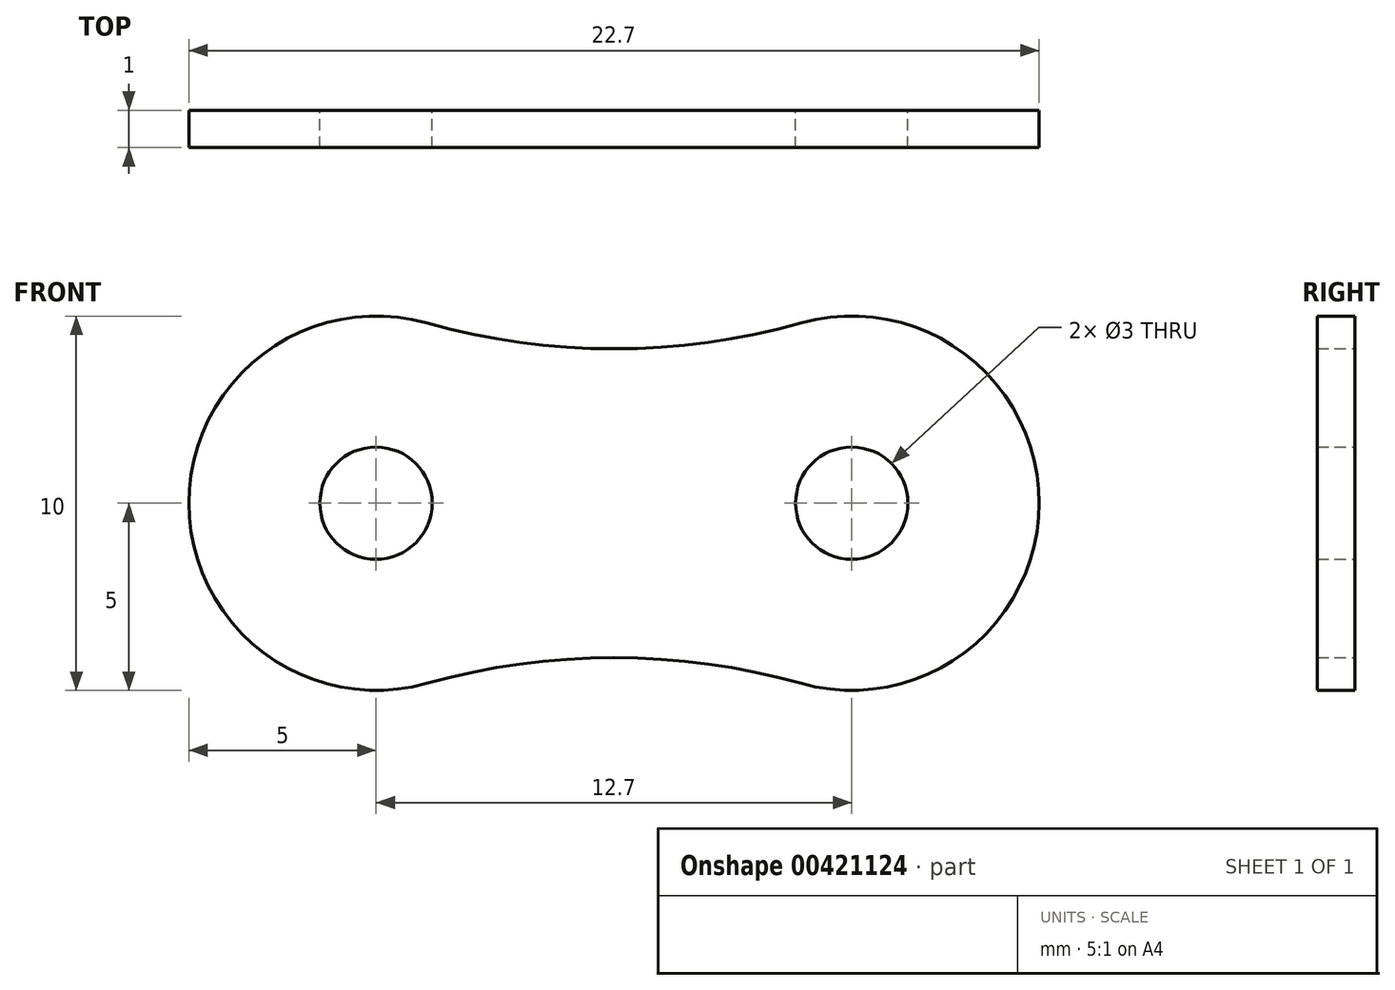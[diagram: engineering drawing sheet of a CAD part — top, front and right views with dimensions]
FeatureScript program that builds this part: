
annotation { "Feature Type Name" : "Feature", "Feature Type Description" : "" }
export const myFeature = defineFeature(function(context is Context, id is Id, definition is map)
    precondition{}
    {
        {
            var Q0;
            Q0=qCreatedBy(makeId("Front.planeOp"),FACE);
            var sketch = newSketch(context, id + "F0", { "sketchPlane" : qUnion([Q0])});
            skArc(sketch, "E0", {"start": v(-5, 4.81) * mm, "mid": v(-11.35, 0) * mm, "end": v(-5, -4.81) * mm});
            skArc(sketch, "E1", {"start": v(-5, 4.81) * mm, "mid": v(0, 4.13) * mm, "end": v(5, 4.81) * mm});
            skArc(sketch, "E2", {"start": v(5, -4.81) * mm, "mid": v(0, -4.13) * mm, "end": v(-5, -4.81) * mm});
            skArc(sketch, "E3", {"start": v(5, -4.81) * mm, "mid": v(11.35, 0) * mm, "end": v(5, 4.81) * mm});
            skCircle(sketch, "E4", {"center": v(-6.35, 0) * mm, "radius": 1.5 * mm});
            skCircle(sketch, "E5", {"center": v(6.35, 0) * mm, "radius": 1.5 * mm});
            skSolve(sketch);
        }
        {
            var Q0;
            Q0=makeQuery(id+"F0.imprint","IMPRINT",FACE,{"disambiguationData":[TD([[makeQuery(id+"F0.imprint","IMPRINT",EDGE,{"derivedFrom":sQuery(id+"F0.wireOp",EDGE,"E0")}),1.0]])]});
            extrude(context, id + "F1", {"entities" : qUnion([Q0]), "depth" : 1 * mm});
        }
    });
